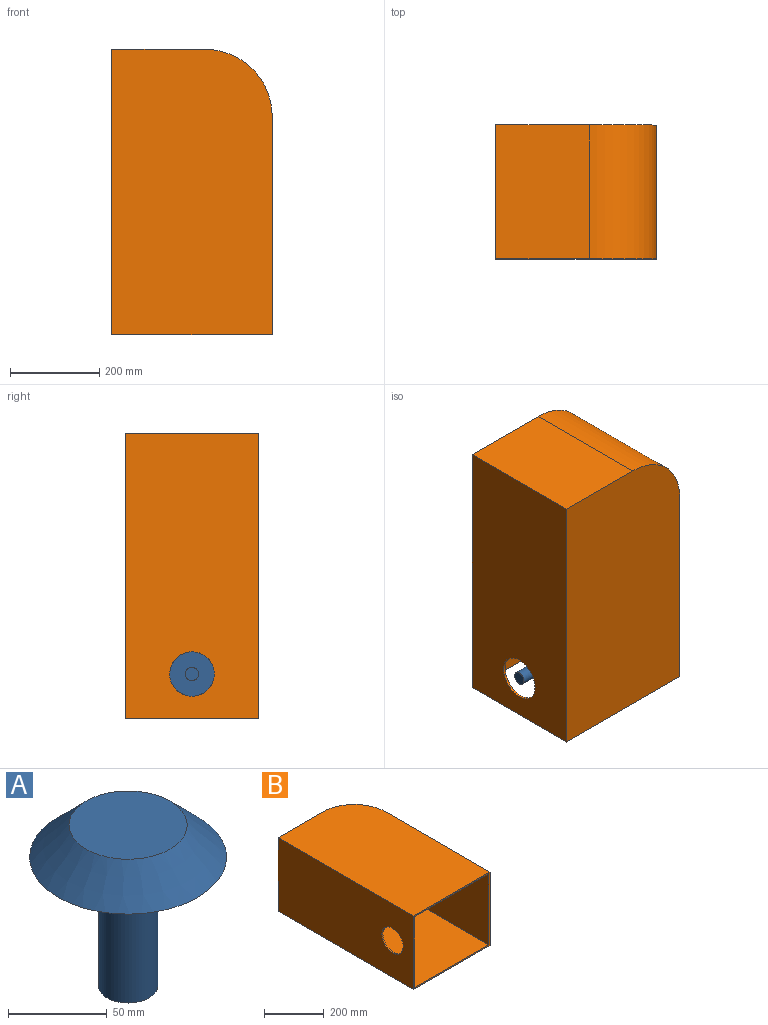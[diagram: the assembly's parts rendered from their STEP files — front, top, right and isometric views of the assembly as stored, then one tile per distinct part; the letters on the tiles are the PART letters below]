
ASSEMBLY  parts=2 mates=2
PART A: 5 faces, bbox 100x100x100 mm
  f0: cone r=50mm half-angle=45deg, axis (0,0,-1), area 7108.6mm2, adj f1,f2
  f1: plane 60x60mm, normal (0,0,1), area 2827.4mm2, adj f0
  f2: plane 100x100mm, normal (0,0,-1), area 7147.1mm2, adj f0,f3
  f3: cylinder r=15mm len=80mm, axis (0,0,1), area 7539.8mm2, adj f2,f4
  f4: plane 30x30mm, normal (0,0,-1), area 706.9mm2, adj f3
PART B: 14 faces, bbox 360x640x300 mm
  f0: plane 360x300mm, normal (0,-1,0), area 6500mm2, adj f2,f3,f5,f6,f8,f9,f11,f12
  f1: plane 300x210mm, normal (0,1,0), area 63000mm2, adj f2,f4,f5,f6
  f2: plane 640x300mm, normal (-1,0,0), area 184146mm2, adj f0,f1,f5,f6,f13
  f3: plane 490x300mm, normal (1,0,0), area 147000mm2, adj f0,f4,f5,f6
  f4: cylinder r=150mm len=300mm, axis (0,0,-1), area 70685.8mm2, adj f1,f3,f5,f6
  f5: plane 640x360mm, normal (0,0,1), area 225571.5mm2, adj f0,f1,f2,f3,f4
  f6: plane 640x360mm, normal (0,0,-1), area 225571.5mm2, adj f0,f1,f2,f3,f4
  f7: plane 290x205mm, normal (0,-1,0), area 59450mm2, adj f8,f10,f11,f12
  f8: plane 635x290mm, normal (1,0,0), area 176296mm2, adj f0,f7,f11,f12,f13
  f9: plane 490x290mm, normal (-1,0,0), area 142100mm2, adj f0,f10,f11,f12
  f10: cylinder r=145mm len=290mm, axis (0,0,-1), area 66052mm2, adj f7,f9,f11,f12
  f11: plane 635x350mm, normal (0,0,-1), area 217738mm2, adj f0,f7,f8,f9,f10
  f12: plane 635x350mm, normal (0,0,1), area 217738mm2, adj f0,f7,f8,f9,f10
  f13: cylinder r=50mm len=100mm, axis (-1,0,0), area 1570.8mm2, adj f2,f8
PLACE A rot(axis=(-0.58,0.58,-0.58),120deg) t=(75,0,100)mm
PLACE B rot(axis=(1,0,0),90deg) t=(-5,0,0)mm
MATE cylindrical A.f0 <-> B.f13  axis (1,0,0) through (35,0,100)mm
MATE fastened A.f0 <-> B.f13  axis (-1,0,0) through (-5,0,100)mm
